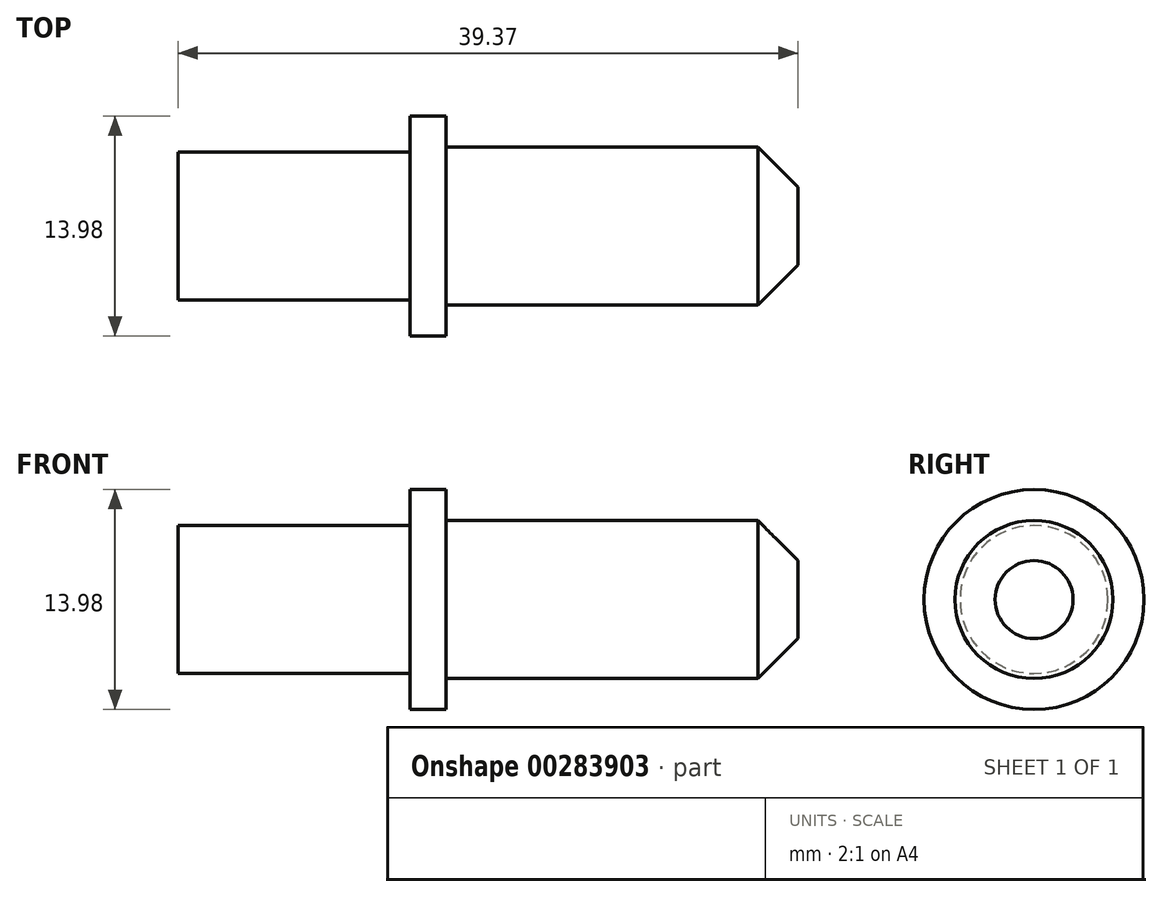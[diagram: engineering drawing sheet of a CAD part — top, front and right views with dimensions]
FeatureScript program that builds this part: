
annotation { "Feature Type Name" : "Feature", "Feature Type Description" : "" }
export const myFeature = defineFeature(function(context is Context, id is Id, definition is map)
    precondition{}
    {
        {
            var Q0;
            Q0=qCreatedBy(makeId("Front.planeOp"),FACE);
            var sketch = newSketch(context, id + "F0", { "sketchPlane" : qUnion([Q0])});
            skLineSegment(sketch, "E0", {"start": v(0, 0) * mm, "end": v(0, 5.02) * mm});
            skLineSegment(sketch, "E1", {"start": v(0, 5.02) * mm, "end": v(-22.35, 5.02) * mm});
            skLineSegment(sketch, "E2", {"start": v(-22.35, 5.02) * mm, "end": v(-22.35, 6.99) * mm});
            skLineSegment(sketch, "E3", {"start": v(-22.35, 6.99) * mm, "end": v(-24.64, 6.99) * mm});
            skLineSegment(sketch, "E4", {"start": v(-24.64, 6.99) * mm, "end": v(-24.64, 4.7) * mm});
            skLineSegment(sketch, "E5", {"start": v(-24.64, 4.7) * mm, "end": v(-39.37, 4.7) * mm});
            skLineSegment(sketch, "E6", {"start": v(-39.37, 4.7) * mm, "end": v(-39.37, 0) * mm});
            skLineSegment(sketch, "E7", {"start": v(-39.37, 0) * mm, "end": v(0, 0) * mm});
            skLineSegment(sketch, "E8", {"start": v(-39.37, 0) * mm, "end": v(-39.37, -4.7) * mm, "construction": true});
            skLineSegment(sketch, "E9", {"start": v(-39.37, -4.7) * mm, "end": v(-24.64, -4.7) * mm, "construction": true});
            skLineSegment(sketch, "E10", {"start": v(-24.64, -4.7) * mm, "end": v(-24.64, -6.99) * mm, "construction": true});
            skLineSegment(sketch, "E11", {"start": v(-24.64, -6.99) * mm, "end": v(-22.35, -6.99) * mm, "construction": true});
            skLineSegment(sketch, "E12", {"start": v(-22.35, -6.99) * mm, "end": v(-22.35, -5.02) * mm, "construction": true});
            skLineSegment(sketch, "E13", {"start": v(-22.35, -5.02) * mm, "end": v(0, -5.02) * mm, "construction": true});
            skLineSegment(sketch, "E14", {"start": v(0, -5.02) * mm, "end": v(0, 0) * mm, "construction": true});
            skSolve(sketch);
        }
        {
            var Q0;
            Q0=makeQuery(id+"F0.imprint","IMPRINT",FACE,{"disambiguationData":[TD([[makeQuery(id+"F0.imprint","IMPRINT",EDGE,{"derivedFrom":sQuery(id+"F0.wireOp",EDGE,"E0")}),1.0]])]});
            var Q1;
            Q1=sQuery(id+"F0.wireOp",EDGE,"E7");
            revolve(context, id + "F1", {"entities" : qUnion([Q0]), "axis" : qUnion([Q1]), "revolveType" : RevolveType.FULL});
        }
        {
            var Q0;
            Q0=makeQuery(id+"F1.opRevolve","SWEPT_EDGE",EDGE,{"disambiguationData":[OSD([sQuery(id+"F0.wireOp",EDGE,"E0"),sQuery(id+"F0.wireOp",EDGE,"E1")])]});
            chamfer(context, id + "F2", {"entities" : qUnion([Q0]), "width" : 2.54 * mm, "tangentPropagation" : true});
        }
    });
